# Revit family: 28610-presto
name_source: partatom
category: Plumbing Fixtures
units: mm (PartAtom-declared; Revit-internal decimal feet)

## family parameters
Always vertical = Yes
Cut with Voids When Loaded = No
Maintain Annotation Orientation = No
OmniClass Number = 23.45.00.00
OmniClass Title = Sanitary, Laundry, and Cleaning Equipment
Part Type = Normal
Room Calculation Point = No
Round Connector Dimension = Use Diameter
Shared = No
Work Plane-Based = Yes

## types (1)
- 28610-presto
    - Hydraulic supply = 20.00 mm
    Default Elevation = 1219 mm
    Description = 28610 - PRESTO 4000 S single control mixer tap
    Manufacturer = presto
    Model = 28610
    RANGE = Deck-mounted mixer tap
    Recommended pressure = 300000.0 Pa
    URL = https://www.prestodatashare.com
    brand = LES ROBINETS PRESTO
    flow = 0.1 L/s
    flow time = 20.0 s
    min pressure = 100000.0 Pa
    pressure = 500000.0 Pa
    ref = 28610 - PRESTO 4000 S single control mixer tap

## geometry (parser evidence)
native form markers: Sweep x5
no freeform markers — native parametric forms only
